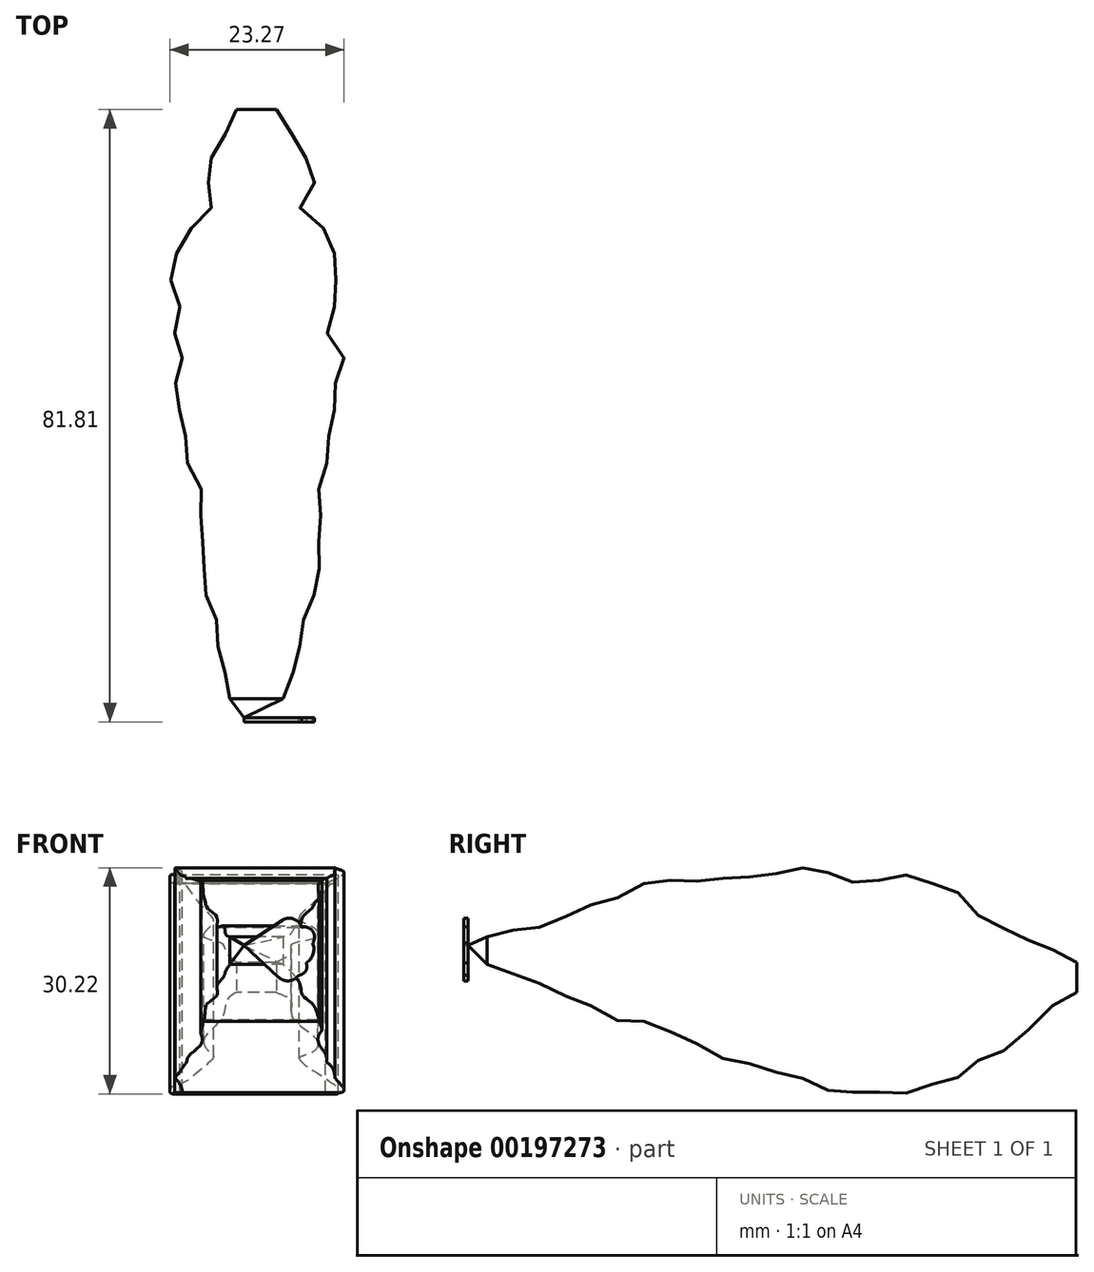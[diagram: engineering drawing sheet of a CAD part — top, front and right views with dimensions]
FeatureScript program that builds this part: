
annotation { "Feature Type Name" : "Feature", "Feature Type Description" : "" }
export const myFeature = defineFeature(function(context is Context, id is Id, definition is map)
    precondition{}
    {
        {
            var Q0;
            Q0=qCreatedBy(makeId("Front.planeOp"),FACE);
            var sketch = newSketch(context, id + "F0", { "sketchPlane" : qUnion([Q0])});
            skLineSegment(sketch, "E0.bottom", {"start": v(-55.22, 4.52) * mm, "end": v(-43.66, 4.52) * mm});
            skLineSegment(sketch, "E0.top", {"start": v(-55.22, -14.22) * mm, "end": v(-43.66, -14.22) * mm});
            skLineSegment(sketch, "E0.left", {"start": v(-55.22, 4.52) * mm, "end": v(-55.22, -14.22) * mm});
            skLineSegment(sketch, "E0.right", {"start": v(-43.66, 4.52) * mm, "end": v(-43.66, -14.22) * mm});
            skSolve(sketch);
        }
        {
            var Q0;
            Q0=qCreatedBy(makeId("Front.planeOp"),FACE);
            cPlane(context, id + "F1", {"entities" : qUnion([Q0]), "cplaneType" : CPlaneType.OFFSET, "offset" : 2.54 * mm, "width" : 152.4 * mm, "height" : 152.4 * mm});
        }
        {
            var Q0;
            Q0=qCreatedBy(id+"F1.planeOp",FACE);
            var sketch = newSketch(context, id + "F2", { "sketchPlane" : qUnion([Q0])});
            skLineSegment(sketch, "E1.bottom", {"start": v(-57.62, 7.3) * mm, "end": v(-41, 7.3) * mm});
            skLineSegment(sketch, "E1.top", {"start": v(-57.62, -16.35) * mm, "end": v(-41, -16.35) * mm});
            skLineSegment(sketch, "E1.left", {"start": v(-57.62, 7.3) * mm, "end": v(-57.62, -16.35) * mm});
            skLineSegment(sketch, "E1.right", {"start": v(-41, 7.3) * mm, "end": v(-41, -16.35) * mm});
            skSolve(sketch);
        }
        {
            var Q0;
            Q0=qCreatedBy(id+"F1.planeOp",FACE);
            cPlane(context, id + "F3", {"entities" : qUnion([Q0]), "cplaneType" : CPlaneType.OFFSET, "offset" : 2.54 * mm, "width" : 152.4 * mm, "height" : 152.4 * mm});
        }
        {
            var Q0;
            Q0=qCreatedBy(id+"F3.planeOp",FACE);
            var sketch = newSketch(context, id + "F4", { "sketchPlane" : qUnion([Q0])});
            skLineSegment(sketch, "E2.bottom", {"start": v(-39.37, 9.18) * mm, "end": v(-59.18, 9.18) * mm});
            skLineSegment(sketch, "E2.top", {"start": v(-39.37, -17.46) * mm, "end": v(-59.18, -17.46) * mm});
            skLineSegment(sketch, "E2.left", {"start": v(-39.37, 9.18) * mm, "end": v(-39.37, -17.46) * mm});
            skLineSegment(sketch, "E2.right", {"start": v(-59.18, 9.18) * mm, "end": v(-59.18, -17.46) * mm});
            skSolve(sketch);
        }
        {
            var Q0;
            Q0=qCreatedBy(id+"F3.planeOp",FACE);
            cPlane(context, id + "F5", {"entities" : qUnion([Q0]), "cplaneType" : CPlaneType.OFFSET, "offset" : 2.54 * mm, "width" : 152.4 * mm, "height" : 152.4 * mm});
        }
        {
            var Q0;
            Q0=qCreatedBy(id+"F5.planeOp",FACE);
            var sketch = newSketch(context, id + "F6", { "sketchPlane" : qUnion([Q0])});
            skLineSegment(sketch, "E3.bottom", {"start": v(-38.88, -17.91) * mm, "end": v(-60.62, -17.91) * mm});
            skLineSegment(sketch, "E3.top", {"start": v(-38.88, 9.23) * mm, "end": v(-60.62, 9.23) * mm});
            skLineSegment(sketch, "E3.left", {"start": v(-38.88, -17.91) * mm, "end": v(-38.88, 9.23) * mm});
            skLineSegment(sketch, "E3.right", {"start": v(-60.62, -17.91) * mm, "end": v(-60.62, 9.23) * mm});
            skSolve(sketch);
        }
        {
            var Q0;
            Q0=qCreatedBy(id+"F5.planeOp",FACE);
            cPlane(context, id + "F7", {"entities" : qUnion([Q0]), "cplaneType" : CPlaneType.OFFSET, "offset" : 2.54 * mm, "width" : 152.4 * mm, "height" : 152.4 * mm});
        }
        {
            var Q0;
            Q0=qCreatedBy(id+"F7.planeOp",FACE);
            var sketch = newSketch(context, id + "F8", { "sketchPlane" : qUnion([Q0])});
            skLineSegment(sketch, "E4.bottom", {"start": v(-60.8, 10.33) * mm, "end": v(-38.76, 10.33) * mm});
            skLineSegment(sketch, "E4.top", {"start": v(-60.8, -18.88) * mm, "end": v(-38.76, -18.88) * mm});
            skLineSegment(sketch, "E4.left", {"start": v(-60.8, 10.33) * mm, "end": v(-60.8, -18.88) * mm});
            skLineSegment(sketch, "E4.right", {"start": v(-38.76, 10.33) * mm, "end": v(-38.76, -18.88) * mm});
            skSolve(sketch);
        }
        {
            var Q0;
            Q0=qCreatedBy(id+"F7.planeOp",FACE);
            cPlane(context, id + "F9", {"entities" : qUnion([Q0]), "cplaneType" : CPlaneType.OFFSET, "offset" : 2.54 * mm, "width" : 152.4 * mm, "height" : 152.4 * mm});
        }
        {
            var Q0;
            Q0=qCreatedBy(id+"F9.planeOp",FACE);
            var sketch = newSketch(context, id + "F10", { "sketchPlane" : qUnion([Q0])});
            skLineSegment(sketch, "E5.bottom", {"start": v(-38.55, 9.84) * mm, "end": v(-59.66, 9.84) * mm});
            skLineSegment(sketch, "E5.top", {"start": v(-38.55, -18.76) * mm, "end": v(-59.66, -18.76) * mm});
            skLineSegment(sketch, "E5.left", {"start": v(-38.55, 9.84) * mm, "end": v(-38.55, -18.76) * mm});
            skLineSegment(sketch, "E5.right", {"start": v(-59.66, 9.84) * mm, "end": v(-59.66, -18.76) * mm});
            skSolve(sketch);
        }
        {
            var Q0;
            Q0=qCreatedBy(id+"F9.planeOp",FACE);
            cPlane(context, id + "F11", {"entities" : qUnion([Q0]), "cplaneType" : CPlaneType.OFFSET, "offset" : 2.54 * mm, "width" : 152.4 * mm, "height" : 152.4 * mm});
        }
        {
            var Q0;
            Q0=qCreatedBy(id+"F11.planeOp",FACE);
            var sketch = newSketch(context, id + "F12", { "sketchPlane" : qUnion([Q0])});
            skLineSegment(sketch, "E6.bottom", {"start": v(-39.98, 9.35) * mm, "end": v(-60.01, 9.35) * mm});
            skLineSegment(sketch, "E6.top", {"start": v(-39.98, -18.7) * mm, "end": v(-60.01, -18.7) * mm});
            skLineSegment(sketch, "E6.left", {"start": v(-39.98, 9.35) * mm, "end": v(-39.98, -18.7) * mm});
            skLineSegment(sketch, "E6.right", {"start": v(-60.01, 9.35) * mm, "end": v(-60.01, -18.7) * mm});
            skSolve(sketch);
        }
        {
            var Q0;
            Q0=qCreatedBy(id+"F11.planeOp",FACE);
            cPlane(context, id + "F13", {"entities" : qUnion([Q0]), "cplaneType" : CPlaneType.OFFSET, "offset" : 2.54 * mm, "width" : 152.4 * mm, "height" : 152.4 * mm});
        }
        {
            var Q0;
            Q0=qCreatedBy(id+"F13.planeOp",FACE);
            var sketch = newSketch(context, id + "F14", { "sketchPlane" : qUnion([Q0])});
            skLineSegment(sketch, "E7.bottom", {"start": v(-39.61, 9.47) * mm, "end": v(-60.23, 9.47) * mm});
            skLineSegment(sketch, "E7.top", {"start": v(-39.61, -18.76) * mm, "end": v(-60.23, -18.76) * mm});
            skLineSegment(sketch, "E7.left", {"start": v(-39.61, 9.47) * mm, "end": v(-39.61, -18.76) * mm});
            skLineSegment(sketch, "E7.right", {"start": v(-60.23, 9.47) * mm, "end": v(-60.23, -18.76) * mm});
            skSolve(sketch);
        }
        {
            var Q0;
            Q0=qCreatedBy(id+"F13.planeOp",FACE);
            cPlane(context, id + "F15", {"entities" : qUnion([Q0]), "cplaneType" : CPlaneType.OFFSET, "offset" : 2.54 * mm, "width" : 152.4 * mm, "height" : 152.4 * mm});
        }
        {
            var Q0;
            Q0=qCreatedBy(id+"F15.planeOp",FACE);
            var sketch = newSketch(context, id + "F16", { "sketchPlane" : qUnion([Q0])});
            skLineSegment(sketch, "E8.bottom", {"start": v(-37.71, 10.54) * mm, "end": v(-59.31, 10.54) * mm});
            skLineSegment(sketch, "E8.top", {"start": v(-37.71, -18.56) * mm, "end": v(-59.31, -18.56) * mm});
            skLineSegment(sketch, "E8.left", {"start": v(-37.71, 10.54) * mm, "end": v(-37.71, -18.56) * mm});
            skLineSegment(sketch, "E8.right", {"start": v(-59.31, 10.54) * mm, "end": v(-59.31, -18.56) * mm});
            skSolve(sketch);
        }
        {
            var Q0;
            Q0=qCreatedBy(id+"F15.planeOp",FACE);
            cPlane(context, id + "F17", {"entities" : qUnion([Q0]), "cplaneType" : CPlaneType.OFFSET, "offset" : 2.54 * mm, "width" : 152.4 * mm, "height" : 152.4 * mm});
        }
        {
            var Q0;
            Q0=qCreatedBy(id+"F17.planeOp",FACE);
            var sketch = newSketch(context, id + "F18", { "sketchPlane" : qUnion([Q0])});
            skLineSegment(sketch, "E9.bottom", {"start": v(-59.97, -17.16) * mm, "end": v(-38.63, -17.16) * mm});
            skLineSegment(sketch, "E9.top", {"start": v(-59.97, 11.13) * mm, "end": v(-38.63, 11.13) * mm});
            skLineSegment(sketch, "E9.left", {"start": v(-59.97, -17.16) * mm, "end": v(-59.97, 11.13) * mm});
            skLineSegment(sketch, "E9.right", {"start": v(-38.63, -17.16) * mm, "end": v(-38.63, 11.13) * mm});
            skSolve(sketch);
        }
        {
            var Q0;
            Q0=qCreatedBy(id+"F17.planeOp",FACE);
            cPlane(context, id + "F19", {"entities" : qUnion([Q0]), "cplaneType" : CPlaneType.OFFSET, "offset" : 2.54 * mm, "width" : 152.4 * mm, "height" : 152.4 * mm});
        }
        {
            var Q0;
            Q0=qCreatedBy(id+"F19.planeOp",FACE);
            cPlane(context, id + "F20", {"entities" : qUnion([Q0]), "cplaneType" : CPlaneType.OFFSET, "offset" : 2.54 * mm, "width" : 152.4 * mm, "height" : 152.4 * mm});
        }
        {
            var Q0;
            Q0=qCreatedBy(id+"F19.planeOp",FACE);
            var sketch = newSketch(context, id + "F21", { "sketchPlane" : qUnion([Q0])});
            skLineSegment(sketch, "E10.bottom", {"start": v(-60.2, -16.65) * mm, "end": v(-38.94, -16.65) * mm});
            skLineSegment(sketch, "E10.top", {"start": v(-60.2, 11.18) * mm, "end": v(-38.94, 11.18) * mm});
            skLineSegment(sketch, "E10.left", {"start": v(-60.2, -16.65) * mm, "end": v(-60.2, 11.18) * mm});
            skLineSegment(sketch, "E10.right", {"start": v(-38.94, -16.65) * mm, "end": v(-38.94, 11.18) * mm});
            skSolve(sketch);
        }
        {
            var Q0;
            Q0=qCreatedBy(id+"F20.planeOp",FACE);
            var sketch = newSketch(context, id + "F22", { "sketchPlane" : qUnion([Q0])});
            skLineSegment(sketch, "E11.bottom", {"start": v(-59.53, -15.85) * mm, "end": v(-39.07, -15.85) * mm});
            skLineSegment(sketch, "E11.top", {"start": v(-59.53, 10.35) * mm, "end": v(-39.07, 10.35) * mm});
            skLineSegment(sketch, "E11.left", {"start": v(-59.53, -15.85) * mm, "end": v(-59.53, 10.35) * mm});
            skLineSegment(sketch, "E11.right", {"start": v(-39.07, -15.85) * mm, "end": v(-39.07, 10.35) * mm});
            skSolve(sketch);
        }
        {
            var Q0;
            Q0=qCreatedBy(id+"F20.planeOp",FACE);
            cPlane(context, id + "F23", {"entities" : qUnion([Q0]), "cplaneType" : CPlaneType.OFFSET, "offset" : 2.54 * mm, "width" : 152.4 * mm, "height" : 152.4 * mm});
        }
        {
            var Q0;
            Q0=qCreatedBy(id+"F23.planeOp",FACE);
            var sketch = newSketch(context, id + "F24", { "sketchPlane" : qUnion([Q0])});
            skLineSegment(sketch, "E12.bottom", {"start": v(-58.95, -14.98) * mm, "end": v(-39.63, -14.98) * mm});
            skLineSegment(sketch, "E12.top", {"start": v(-58.95, 10.1) * mm, "end": v(-39.63, 10.1) * mm});
            skLineSegment(sketch, "E12.left", {"start": v(-58.95, -14.98) * mm, "end": v(-58.95, 10.1) * mm});
            skLineSegment(sketch, "E12.right", {"start": v(-39.63, -14.98) * mm, "end": v(-39.63, 10.1) * mm});
            skSolve(sketch);
        }
        {
            var Q0;
            Q0=qCreatedBy(id+"F23.planeOp",FACE);
            cPlane(context, id + "F25", {"entities" : qUnion([Q0]), "cplaneType" : CPlaneType.OFFSET, "offset" : 2.54 * mm, "width" : 152.4 * mm, "height" : 152.4 * mm});
        }
        {
            var Q0;
            Q0=qCreatedBy(id+"F25.planeOp",FACE);
            var sketch = newSketch(context, id + "F26", { "sketchPlane" : qUnion([Q0])});
            skLineSegment(sketch, "E13.bottom", {"start": v(-58.7, -14.62) * mm, "end": v(-40.03, -14.62) * mm});
            skLineSegment(sketch, "E13.top", {"start": v(-58.7, 9.76) * mm, "end": v(-40.03, 9.76) * mm});
            skLineSegment(sketch, "E13.left", {"start": v(-58.7, -14.62) * mm, "end": v(-58.7, 9.76) * mm});
            skLineSegment(sketch, "E13.right", {"start": v(-40.03, -14.62) * mm, "end": v(-40.03, 9.76) * mm});
            skSolve(sketch);
        }
        {
            var Q0;
            Q0=qCreatedBy(id+"F25.planeOp",FACE);
            cPlane(context, id + "F27", {"entities" : qUnion([Q0]), "cplaneType" : CPlaneType.OFFSET, "offset" : 2.54 * mm, "width" : 152.4 * mm, "height" : 152.4 * mm});
        }
        {
            var Q0;
            Q0=qCreatedBy(id+"F27.planeOp",FACE);
            var sketch = newSketch(context, id + "F28", { "sketchPlane" : qUnion([Q0])});
            skLineSegment(sketch, "E14.bottom", {"start": v(-58.28, -13.75) * mm, "end": v(-40.1, -13.75) * mm});
            skLineSegment(sketch, "E14.top", {"start": v(-58.28, 9.86) * mm, "end": v(-40.1, 9.86) * mm});
            skLineSegment(sketch, "E14.left", {"start": v(-58.28, -13.75) * mm, "end": v(-58.28, 9.86) * mm});
            skLineSegment(sketch, "E14.right", {"start": v(-40.1, -13.75) * mm, "end": v(-40.1, 9.86) * mm});
            skSolve(sketch);
        }
        {
            var Q0;
            Q0=qCreatedBy(id+"F27.planeOp",FACE);
            cPlane(context, id + "F29", {"entities" : qUnion([Q0]), "cplaneType" : CPlaneType.OFFSET, "offset" : 2.54 * mm, "width" : 152.4 * mm, "height" : 152.4 * mm});
        }
        {
            var Q0;
            Q0=qCreatedBy(id+"F29.planeOp",FACE);
            var sketch = newSketch(context, id + "F30", { "sketchPlane" : qUnion([Q0])});
            skLineSegment(sketch, "E15.bottom", {"start": v(-56.71, -12.18) * mm, "end": v(-41.08, -12.18) * mm});
            skLineSegment(sketch, "E15.top", {"start": v(-56.71, 9.43) * mm, "end": v(-41.08, 9.43) * mm});
            skLineSegment(sketch, "E15.left", {"start": v(-56.71, -12.18) * mm, "end": v(-56.71, 9.43) * mm});
            skLineSegment(sketch, "E15.right", {"start": v(-41.08, -12.18) * mm, "end": v(-41.08, 9.43) * mm});
            skSolve(sketch);
        }
        {
            var Q0;
            Q0=qCreatedBy(id+"F29.planeOp",FACE);
            var Q1;
            Q1 = qBodyType(qCreatedBy(id + "F32" ,EDGE), BodyType.WIRE);
            cPlane(context, id + "F31", {"entities" : qUnion([Q0, Q1]), "cplaneType" : CPlaneType.OFFSET, "offset" : 2.54 * mm, "width" : 152.4 * mm, "height" : 152.4 * mm});
        }
        {
            var Q0;
            Q0=qCreatedBy(id+"F31.planeOp",FACE);
            var sketch = newSketch(context, id + "F32", { "sketchPlane" : qUnion([Q0])});
            skLineSegment(sketch, "E16.bottom", {"start": v(-56.81, -10.9) * mm, "end": v(-40.98, -10.9) * mm});
            skLineSegment(sketch, "E16.top", {"start": v(-56.81, 9.56) * mm, "end": v(-40.98, 9.56) * mm});
            skLineSegment(sketch, "E16.left", {"start": v(-56.81, -10.9) * mm, "end": v(-56.81, 9.56) * mm});
            skLineSegment(sketch, "E16.right", {"start": v(-40.98, -10.9) * mm, "end": v(-40.98, 9.56) * mm});
            skSolve(sketch);
        }
        {
            var Q0;
            Q0=qCreatedBy(id+"F31.planeOp",FACE);
            cPlane(context, id + "F33", {"entities" : qUnion([Q0]), "cplaneType" : CPlaneType.OFFSET, "offset" : 2.54 * mm, "width" : 152.4 * mm, "height" : 152.4 * mm});
        }
        {
            var Q0;
            Q0=qCreatedBy(id+"F33.planeOp",FACE);
            var sketch = newSketch(context, id + "F34", { "sketchPlane" : qUnion([Q0])});
            skLineSegment(sketch, "E17.bottom", {"start": v(-40.67, 9.48) * mm, "end": v(-56.64, 9.48) * mm});
            skLineSegment(sketch, "E17.top", {"start": v(-40.67, -10.2) * mm, "end": v(-56.64, -10.2) * mm});
            skLineSegment(sketch, "E17.left", {"start": v(-40.67, 9.48) * mm, "end": v(-40.67, -10.2) * mm});
            skLineSegment(sketch, "E17.right", {"start": v(-56.64, 9.48) * mm, "end": v(-56.64, -10.2) * mm});
            skSolve(sketch);
        }
        {
            var Q0;
            Q0=qCreatedBy(id+"F33.planeOp",FACE);
            cPlane(context, id + "F35", {"entities" : qUnion([Q0]), "cplaneType" : CPlaneType.OFFSET, "offset" : 2.54 * mm, "width" : 152.4 * mm, "height" : 152.4 * mm});
        }
        {
            var Q0;
            Q0=qCreatedBy(id+"F35.planeOp",FACE);
            var sketch = newSketch(context, id + "F36", { "sketchPlane" : qUnion([Q0])});
            skLineSegment(sketch, "E18.bottom", {"start": v(-41.15, 8.93) * mm, "end": v(-56.56, 8.93) * mm});
            skLineSegment(sketch, "E18.top", {"start": v(-41.15, -9.09) * mm, "end": v(-56.56, -9.09) * mm});
            skLineSegment(sketch, "E18.left", {"start": v(-41.15, 8.93) * mm, "end": v(-41.15, -9.09) * mm});
            skLineSegment(sketch, "E18.right", {"start": v(-56.56, 8.93) * mm, "end": v(-56.56, -9.09) * mm});
            skSolve(sketch);
        }
        {
            var Q0;
            Q0=qCreatedBy(id+"F35.planeOp",FACE);
            cPlane(context, id + "F37", {"entities" : qUnion([Q0]), "cplaneType" : CPlaneType.OFFSET, "offset" : 2.54 * mm, "width" : 152.4 * mm, "height" : 152.4 * mm});
        }
        {
            var Q0;
            Q0=qCreatedBy(id+"F37.planeOp",FACE);
            var sketch = newSketch(context, id + "F38", { "sketchPlane" : qUnion([Q0])});
            skLineSegment(sketch, "E19.bottom", {"start": v(-40.99, 7.37) * mm, "end": v(-56.4, 7.37) * mm});
            skLineSegment(sketch, "E19.top", {"start": v(-40.99, -9.24) * mm, "end": v(-56.4, -9.24) * mm});
            skLineSegment(sketch, "E19.left", {"start": v(-40.99, 7.37) * mm, "end": v(-40.99, -9.24) * mm});
            skLineSegment(sketch, "E19.right", {"start": v(-56.4, 7.37) * mm, "end": v(-56.4, -9.24) * mm});
            skSolve(sketch);
        }
        {
            var Q0;
            Q0=qCreatedBy(id+"F37.planeOp",FACE);
            cPlane(context, id + "F39", {"entities" : qUnion([Q0]), "cplaneType" : CPlaneType.OFFSET, "offset" : 2.54 * mm, "width" : 152.4 * mm, "height" : 152.4 * mm});
        }
        {
            var Q0;
            Q0=qCreatedBy(id+"F39.planeOp",FACE);
            var sketch = newSketch(context, id + "F40", { "sketchPlane" : qUnion([Q0])});
            skLineSegment(sketch, "E20.bottom", {"start": v(-41.44, 6.78) * mm, "end": v(-56.23, 6.78) * mm});
            skLineSegment(sketch, "E20.top", {"start": v(-41.44, -7.76) * mm, "end": v(-56.23, -7.76) * mm});
            skLineSegment(sketch, "E20.left", {"start": v(-41.44, 6.78) * mm, "end": v(-41.44, -7.76) * mm});
            skLineSegment(sketch, "E20.right", {"start": v(-56.23, 6.78) * mm, "end": v(-56.23, -7.76) * mm});
            skSolve(sketch);
        }
        {
            var Q0;
            Q0=qCreatedBy(id+"F39.planeOp",FACE);
            cPlane(context, id + "F41", {"entities" : qUnion([Q0]), "cplaneType" : CPlaneType.OFFSET, "offset" : 2.54 * mm, "width" : 152.4 * mm, "height" : 152.4 * mm});
        }
        {
            var Q0;
            Q0=qCreatedBy(id+"F41.planeOp",FACE);
            var sketch = newSketch(context, id + "F42", { "sketchPlane" : qUnion([Q0])});
            skLineSegment(sketch, "E21.bottom", {"start": v(-42.05, 5.8) * mm, "end": v(-55.87, 5.8) * mm});
            skLineSegment(sketch, "E21.top", {"start": v(-42.05, -6.79) * mm, "end": v(-55.87, -6.79) * mm});
            skLineSegment(sketch, "E21.left", {"start": v(-42.05, 5.8) * mm, "end": v(-42.05, -6.79) * mm});
            skLineSegment(sketch, "E21.right", {"start": v(-55.87, 5.8) * mm, "end": v(-55.87, -6.79) * mm});
            skSolve(sketch);
        }
        {
            var Q0;
            Q0=qCreatedBy(id+"F41.planeOp",FACE);
            cPlane(context, id + "F43", {"entities" : qUnion([Q0]), "cplaneType" : CPlaneType.OFFSET, "offset" : 2.54 * mm, "width" : 152.4 * mm, "height" : 152.4 * mm});
        }
        {
            var Q0;
            Q0=qCreatedBy(id+"F43.planeOp",FACE);
            var sketch = newSketch(context, id + "F44", { "sketchPlane" : qUnion([Q0])});
            skLineSegment(sketch, "E22.bottom", {"start": v(-43.28, 4.58) * mm, "end": v(-54.64, 4.58) * mm});
            skLineSegment(sketch, "E22.top", {"start": v(-43.28, -5.69) * mm, "end": v(-54.64, -5.69) * mm});
            skLineSegment(sketch, "E22.left", {"start": v(-43.28, 4.58) * mm, "end": v(-43.28, -5.69) * mm});
            skLineSegment(sketch, "E22.right", {"start": v(-54.64, 4.58) * mm, "end": v(-54.64, -5.69) * mm});
            skSolve(sketch);
        }
        {
            var Q0;
            Q0=qCreatedBy(id+"F43.planeOp",FACE);
            cPlane(context, id + "F45", {"entities" : qUnion([Q0]), "cplaneType" : CPlaneType.OFFSET, "offset" : 2.54 * mm, "width" : 152.4 * mm, "height" : 152.4 * mm});
        }
        {
            var Q0;
            Q0=qCreatedBy(id+"F45.planeOp",FACE);
            var sketch = newSketch(context, id + "F46", { "sketchPlane" : qUnion([Q0])});
            skLineSegment(sketch, "E23.bottom", {"start": v(-43.52, 3.36) * mm, "end": v(-54.64, 3.36) * mm});
            skLineSegment(sketch, "E23.top", {"start": v(-43.52, -4.46) * mm, "end": v(-54.64, -4.46) * mm});
            skLineSegment(sketch, "E23.left", {"start": v(-43.52, 3.36) * mm, "end": v(-43.52, -4.46) * mm});
            skLineSegment(sketch, "E23.right", {"start": v(-54.64, 3.36) * mm, "end": v(-54.64, -4.46) * mm});
            skSolve(sketch);
        }
        {
            var Q0;
            Q0=qCreatedBy(id+"F45.planeOp",FACE);
            cPlane(context, id + "F47", {"entities" : qUnion([Q0]), "cplaneType" : CPlaneType.OFFSET, "offset" : 2.54 * mm, "width" : 152.4 * mm, "height" : 152.4 * mm});
        }
        {
            var Q0;
            Q0=qCreatedBy(id+"F47.planeOp",FACE);
            var sketch = newSketch(context, id + "F48", { "sketchPlane" : qUnion([Q0])});
            skLineSegment(sketch, "E24.bottom", {"start": v(-44.13, 3.48) * mm, "end": v(-53.79, 3.48) * mm});
            skLineSegment(sketch, "E24.top", {"start": v(-44.13, -3.36) * mm, "end": v(-53.79, -3.36) * mm});
            skLineSegment(sketch, "E24.left", {"start": v(-44.13, 3.48) * mm, "end": v(-44.13, -3.36) * mm});
            skLineSegment(sketch, "E24.right", {"start": v(-53.79, 3.48) * mm, "end": v(-53.79, -3.36) * mm});
            skSolve(sketch);
        }
        {
            var Q0;
            Q0=qCreatedBy(id+"F47.planeOp",FACE);
            cPlane(context, id + "F49", {"entities" : qUnion([Q0]), "cplaneType" : CPlaneType.OFFSET, "offset" : 2.54 * mm, "width" : 152.4 * mm, "height" : 152.4 * mm});
        }
        {
            var Q0;
            Q0=qCreatedBy(id+"F49.planeOp",FACE);
            var sketch = newSketch(context, id + "F50", { "sketchPlane" : qUnion([Q0])});
            skLineSegment(sketch, "E25.bottom", {"start": v(-44.74, 2.5) * mm, "end": v(-53.54, 2.5) * mm});
            skLineSegment(sketch, "E25.top", {"start": v(-44.74, -2.63) * mm, "end": v(-53.54, -2.63) * mm});
            skLineSegment(sketch, "E25.left", {"start": v(-44.74, 2.5) * mm, "end": v(-44.74, -2.63) * mm});
            skLineSegment(sketch, "E25.right", {"start": v(-53.54, 2.5) * mm, "end": v(-53.54, -2.63) * mm});
            skSolve(sketch);
        }
        {
            var Q0;
            Q0=qCreatedBy(id+"F49.planeOp",FACE);
            cPlane(context, id + "F51", {"entities" : qUnion([Q0]), "cplaneType" : CPlaneType.OFFSET, "offset" : 2.54 * mm, "width" : 152.4 * mm, "height" : 152.4 * mm});
        }
        {
            var Q0;
            Q0=qCreatedBy(id+"F51.planeOp",FACE);
            var sketch = newSketch(context, id + "F52", { "sketchPlane" : qUnion([Q0])});
            skLineSegment(sketch, "E26.bottom", {"start": v(-45.84, 2.02) * mm, "end": v(-52.93, 2.02) * mm});
            skLineSegment(sketch, "E26.top", {"start": v(-45.84, -1.65) * mm, "end": v(-52.93, -1.65) * mm});
            skLineSegment(sketch, "E26.left", {"start": v(-45.84, 2.02) * mm, "end": v(-45.84, -1.65) * mm});
            skLineSegment(sketch, "E26.right", {"start": v(-52.93, 2.02) * mm, "end": v(-52.93, -1.65) * mm});
            skSolve(sketch);
        }
        {
            var Q0;
            Q0=qCreatedBy(makeId("Front.planeOp"),FACE);
            cPlane(context, id + "F53", {"entities" : qUnion([Q0]), "cplaneType" : CPlaneType.OFFSET, "offset" : 2.54 * mm, "oppositeDirection" : true, "width" : 152.4 * mm, "height" : 152.4 * mm});
        }
        {
            var Q0;
            Q0=qCreatedBy(id+"F53.planeOp",FACE);
            var sketch = newSketch(context, id + "F54", { "sketchPlane" : qUnion([Q0])});
            skLineSegment(sketch, "E27.bottom", {"start": v(-55.62, 3.36) * mm, "end": v(-41.93, 3.36) * mm});
            skLineSegment(sketch, "E27.top", {"start": v(-55.62, -13.39) * mm, "end": v(-41.93, -13.39) * mm});
            skLineSegment(sketch, "E27.left", {"start": v(-55.62, 3.36) * mm, "end": v(-55.62, -13.39) * mm});
            skLineSegment(sketch, "E27.right", {"start": v(-41.93, 3.36) * mm, "end": v(-41.93, -13.39) * mm});
            skSolve(sketch);
        }
        {
            var Q0;
            Q0=qCreatedBy(id+"F53.planeOp",FACE);
            cPlane(context, id + "F55", {"entities" : qUnion([Q0]), "cplaneType" : CPlaneType.OFFSET, "offset" : 2.54 * mm, "oppositeDirection" : true, "width" : 152.4 * mm, "height" : 152.4 * mm});
        }
        {
            var Q0;
            Q0=qCreatedBy(id+"F55.planeOp",FACE);
            var sketch = newSketch(context, id + "F56", { "sketchPlane" : qUnion([Q0])});
            skLineSegment(sketch, "E28.bottom", {"start": v(-56.36, 2.02) * mm, "end": v(-41.44, 2.02) * mm});
            skLineSegment(sketch, "E28.top", {"start": v(-56.36, -11.55) * mm, "end": v(-41.44, -11.55) * mm});
            skLineSegment(sketch, "E28.left", {"start": v(-56.36, 2.02) * mm, "end": v(-56.36, -11.55) * mm});
            skLineSegment(sketch, "E28.right", {"start": v(-41.44, 2.02) * mm, "end": v(-41.44, -11.55) * mm});
            skSolve(sketch);
        }
        {
            var Q0;
            Q0=qCreatedBy(id+"F55.planeOp",FACE);
            cPlane(context, id + "F57", {"entities" : qUnion([Q0]), "cplaneType" : CPlaneType.OFFSET, "offset" : 2.54 * mm, "oppositeDirection" : true, "width" : 152.4 * mm, "height" : 152.4 * mm});
        }
        {
            var Q0;
            Q0=qCreatedBy(id+"F57.planeOp",FACE);
            var sketch = newSketch(context, id + "F58", { "sketchPlane" : qUnion([Q0])});
            skLineSegment(sketch, "E29.bottom", {"start": v(-54.03, 1.16) * mm, "end": v(-44.5, 1.16) * mm});
            skLineSegment(sketch, "E29.top", {"start": v(-54.03, -8.86) * mm, "end": v(-44.5, -8.86) * mm});
            skLineSegment(sketch, "E29.left", {"start": v(-54.03, 1.16) * mm, "end": v(-54.03, -8.86) * mm});
            skLineSegment(sketch, "E29.right", {"start": v(-44.5, 1.16) * mm, "end": v(-44.5, -8.86) * mm});
            skSolve(sketch);
        }
        {
            var Q0;
            Q0=qCreatedBy(id+"F57.planeOp",FACE);
            cPlane(context, id + "F59", {"entities" : qUnion([Q0]), "cplaneType" : CPlaneType.OFFSET, "offset" : 2.54 * mm, "oppositeDirection" : true, "width" : 152.4 * mm, "height" : 152.4 * mm});
        }
        {
            var Q0;
            Q0=qCreatedBy(id+"F59.planeOp",FACE);
            var sketch = newSketch(context, id + "F60", { "sketchPlane" : qUnion([Q0])});
            skLineSegment(sketch, "E30.bottom", {"start": v(-53.42, 0) * mm, "end": v(-44.74, 0) * mm});
            skLineSegment(sketch, "E30.top", {"start": v(-53.42, -6.66) * mm, "end": v(-44.74, -6.66) * mm});
            skLineSegment(sketch, "E30.left", {"start": v(-53.42, 0) * mm, "end": v(-53.42, -6.66) * mm});
            skLineSegment(sketch, "E30.right", {"start": v(-44.74, 0) * mm, "end": v(-44.74, -6.66) * mm});
            skSolve(sketch);
        }
        {
            var Q0;
            Q0=qCreatedBy(id+"F59.planeOp",FACE);
            cPlane(context, id + "F61", {"entities" : qUnion([Q0]), "cplaneType" : CPlaneType.OFFSET, "offset" : 2.54 * mm, "oppositeDirection" : true, "width" : 152.4 * mm, "height" : 152.4 * mm});
        }
        {
            var Q0;
            Q0=qCreatedBy(id+"F61.planeOp",FACE);
            var sketch = newSketch(context, id + "F62", { "sketchPlane" : qUnion([Q0])});
            skLineSegment(sketch, "E31.bottom", {"start": v(-46.74, -1.36) * mm, "end": v(-52.08, -1.36) * mm});
            skLineSegment(sketch, "E31.top", {"start": v(-46.74, -5.4) * mm, "end": v(-52.08, -5.4) * mm});
            skLineSegment(sketch, "E31.left", {"start": v(-46.74, -1.36) * mm, "end": v(-46.74, -5.4) * mm});
            skLineSegment(sketch, "E31.right", {"start": v(-52.08, -1.36) * mm, "end": v(-52.08, -5.4) * mm});
            skSolve(sketch);
        }
        {
            var Q0;
            Q0=qCreatedBy(id+"F51.planeOp",FACE);
            cPlane(context, id + "F63", {"entities" : qUnion([Q0]), "cplaneType" : CPlaneType.OFFSET, "offset" : 2.54 * mm, "width" : 152.4 * mm, "height" : 152.4 * mm});
        }
        {
            var Q0;
            Q0=qCreatedBy(id+"F63.planeOp",FACE);
            var sketch = newSketch(context, id + "F64", { "sketchPlane" : qUnion([Q0])});
            skLineSegment(sketch, "E32", {"start": v(-51.07, 0.87) * mm, "end": v(-43.4, 3.3) * mm});
            skLineSegment(sketch, "E33", {"start": v(-51.07, 0.87) * mm, "end": v(-41.87, 1.22) * mm});
            skLineSegment(sketch, "E34", {"start": v(-51.07, 0.87) * mm, "end": v(-42.74, -1.44) * mm});
            skLineSegment(sketch, "E35", {"start": v(-51.07, 0.87) * mm, "end": v(-46.44, -3.36) * mm});
            skLineSegment(sketch, "E36", {"start": v(-51.07, 0.87) * mm, "end": v(-43.72, -3.1) * mm});
            skArc(sketch, "E37", {"start": v(-41.87, 1.22) * mm, "mid": v(-41.89, 2.8) * mm, "end": v(-43.4, 3.3) * mm});
            skArc(sketch, "E38", {"start": v(-42.74, -1.44) * mm, "mid": v(-41.84, -0.26) * mm, "end": v(-41.87, 1.22) * mm});
            skArc(sketch, "E39", {"start": v(-43.72, -3.1) * mm, "mid": v(-42.82, -2.5) * mm, "end": v(-42.74, -1.44) * mm});
            skArc(sketch, "E40", {"start": v(-46.44, -3.36) * mm, "mid": v(-45.02, -3.84) * mm, "end": v(-43.72, -3.1) * mm});
            skLineSegment(sketch, "E41", {"start": v(-51.07, 0.87) * mm, "end": v(-45.9, 4.26) * mm});
            skArc(sketch, "E42", {"start": v(-43.4, 3.3) * mm, "mid": v(-44.4, 4.42) * mm, "end": v(-45.9, 4.26) * mm});
            skSolve(sketch);
        }
        {
            var Q0;
            Q0=makeQuery(id+"F62.imprint","IMPRINT",FACE,{"disambiguationData":[TD([[makeQuery(id+"F62.imprint","IMPRINT",EDGE,{"derivedFrom":sQuery(id+"F62.wireOp",EDGE,"E31.bottom")}),1.0]])]});
            var Q1;
            Q1=makeQuery(id+"F60.imprint","IMPRINT",FACE,{"disambiguationData":[TD([[makeQuery(id+"F60.imprint","IMPRINT",EDGE,{"derivedFrom":sQuery(id+"F60.wireOp",EDGE,"E30.bottom")}),-1.0]])]});
            var Q2;
            Q2=makeQuery(id+"F58.imprint","IMPRINT",FACE,{"disambiguationData":[TD([[makeQuery(id+"F58.imprint","IMPRINT",EDGE,{"derivedFrom":sQuery(id+"F58.wireOp",EDGE,"E29.bottom")}),-1.0]])]});
            var Q3;
            Q3=makeQuery(id+"F56.imprint","IMPRINT",FACE,{"disambiguationData":[TD([[makeQuery(id+"F56.imprint","IMPRINT",EDGE,{"derivedFrom":sQuery(id+"F56.wireOp",EDGE,"E28.bottom")}),-1.0]])]});
            var Q4;
            Q4=makeQuery(id+"F54.imprint","IMPRINT",FACE,{"disambiguationData":[TD([[makeQuery(id+"F54.imprint","IMPRINT",EDGE,{"derivedFrom":sQuery(id+"F54.wireOp",EDGE,"E27.bottom")}),-1.0]])]});
            var Q5;
            Q5=makeQuery(id+"F0.imprint","IMPRINT",FACE,{"disambiguationData":[TD([[makeQuery(id+"F0.imprint","IMPRINT",EDGE,{"derivedFrom":sQuery(id+"F0.wireOp",EDGE,"E0.bottom")}),-1.0]])]});
            var Q6;
            Q6=makeQuery(id+"F2.imprint","IMPRINT",FACE,{"disambiguationData":[TD([[makeQuery(id+"F2.imprint","IMPRINT",EDGE,{"derivedFrom":sQuery(id+"F2.wireOp",EDGE,"E1.bottom")}),-1.0]])]});
            var Q7;
            Q7=makeQuery(id+"F4.imprint","IMPRINT",FACE,{"disambiguationData":[TD([[makeQuery(id+"F4.imprint","IMPRINT",EDGE,{"derivedFrom":sQuery(id+"F4.wireOp",EDGE,"E2.bottom")}),1.0]])]});
            var Q8;
            Q8=makeQuery(id+"F6.imprint","IMPRINT",FACE,{"disambiguationData":[TD([[makeQuery(id+"F6.imprint","IMPRINT",EDGE,{"derivedFrom":sQuery(id+"F6.wireOp",EDGE,"E3.bottom")}),-1.0]])]});
            var Q9;
            Q9=makeQuery(id+"F8.imprint","IMPRINT",FACE,{"disambiguationData":[TD([[makeQuery(id+"F8.imprint","IMPRINT",EDGE,{"derivedFrom":sQuery(id+"F8.wireOp",EDGE,"E4.bottom")}),-1.0]])]});
            var Q10;
            Q10=makeQuery(id+"F10.imprint","IMPRINT",FACE,{"disambiguationData":[TD([[makeQuery(id+"F10.imprint","IMPRINT",EDGE,{"derivedFrom":sQuery(id+"F10.wireOp",EDGE,"E5.bottom")}),1.0]])]});
            var Q11;
            Q11=makeQuery(id+"F12.imprint","IMPRINT",FACE,{"disambiguationData":[TD([[makeQuery(id+"F12.imprint","IMPRINT",EDGE,{"derivedFrom":sQuery(id+"F12.wireOp",EDGE,"E6.bottom")}),1.0]])]});
            var Q12;
            Q12=makeQuery(id+"F14.imprint","IMPRINT",FACE,{"disambiguationData":[TD([[makeQuery(id+"F14.imprint","IMPRINT",EDGE,{"derivedFrom":sQuery(id+"F14.wireOp",EDGE,"E7.bottom")}),1.0]])]});
            var Q13;
            Q13=makeQuery(id+"F16.imprint","IMPRINT",FACE,{"disambiguationData":[TD([[makeQuery(id+"F16.imprint","IMPRINT",EDGE,{"derivedFrom":sQuery(id+"F16.wireOp",EDGE,"E8.bottom")}),1.0]])]});
            var Q14;
            Q14=makeQuery(id+"F18.imprint","IMPRINT",FACE,{"disambiguationData":[TD([[makeQuery(id+"F18.imprint","IMPRINT",EDGE,{"derivedFrom":sQuery(id+"F18.wireOp",EDGE,"E9.bottom")}),1.0]])]});
            var Q15;
            Q15=makeQuery(id+"F21.imprint","IMPRINT",FACE,{"disambiguationData":[TD([[makeQuery(id+"F21.imprint","IMPRINT",EDGE,{"derivedFrom":sQuery(id+"F21.wireOp",EDGE,"E10.bottom")}),1.0]])]});
            var Q16;
            Q16=makeQuery(id+"F22.imprint","IMPRINT",FACE,{"disambiguationData":[TD([[makeQuery(id+"F22.imprint","IMPRINT",EDGE,{"derivedFrom":sQuery(id+"F22.wireOp",EDGE,"E11.bottom")}),1.0]])]});
            var Q17;
            Q17=makeQuery(id+"F24.imprint","IMPRINT",FACE,{"disambiguationData":[TD([[makeQuery(id+"F24.imprint","IMPRINT",EDGE,{"derivedFrom":sQuery(id+"F24.wireOp",EDGE,"E12.bottom")}),1.0]])]});
            var Q18;
            Q18=makeQuery(id+"F26.imprint","IMPRINT",FACE,{"disambiguationData":[TD([[makeQuery(id+"F26.imprint","IMPRINT",EDGE,{"derivedFrom":sQuery(id+"F26.wireOp",EDGE,"E13.bottom")}),1.0]])]});
            var Q19;
            Q19=makeQuery(id+"F28.imprint","IMPRINT",FACE,{"disambiguationData":[TD([[makeQuery(id+"F28.imprint","IMPRINT",EDGE,{"derivedFrom":sQuery(id+"F28.wireOp",EDGE,"E14.bottom")}),1.0]])]});
            var Q20;
            Q20=makeQuery(id+"F30.imprint","IMPRINT",FACE,{"disambiguationData":[TD([[makeQuery(id+"F30.imprint","IMPRINT",EDGE,{"derivedFrom":sQuery(id+"F30.wireOp",EDGE,"E15.bottom")}),1.0]])]});
            var Q21;
            Q21=makeQuery(id+"F32.imprint","IMPRINT",FACE,{"disambiguationData":[TD([[makeQuery(id+"F32.imprint","IMPRINT",EDGE,{"derivedFrom":sQuery(id+"F32.wireOp",EDGE,"E16.bottom")}),1.0]])]});
            var Q22;
            Q22=makeQuery(id+"F34.imprint","IMPRINT",FACE,{"disambiguationData":[TD([[makeQuery(id+"F34.imprint","IMPRINT",EDGE,{"derivedFrom":sQuery(id+"F34.wireOp",EDGE,"E17.bottom")}),1.0]])]});
            var Q23;
            Q23=makeQuery(id+"F36.imprint","IMPRINT",FACE,{"disambiguationData":[TD([[makeQuery(id+"F36.imprint","IMPRINT",EDGE,{"derivedFrom":sQuery(id+"F36.wireOp",EDGE,"E18.bottom")}),1.0]])]});
            var Q24;
            Q24=makeQuery(id+"F38.imprint","IMPRINT",FACE,{"disambiguationData":[TD([[makeQuery(id+"F38.imprint","IMPRINT",EDGE,{"derivedFrom":sQuery(id+"F38.wireOp",EDGE,"E19.bottom")}),1.0]])]});
            var Q25;
            Q25=makeQuery(id+"F40.imprint","IMPRINT",FACE,{"disambiguationData":[TD([[makeQuery(id+"F40.imprint","IMPRINT",EDGE,{"derivedFrom":sQuery(id+"F40.wireOp",EDGE,"E20.bottom")}),1.0]])]});
            var Q26;
            Q26=makeQuery(id+"F42.imprint","IMPRINT",FACE,{"disambiguationData":[TD([[makeQuery(id+"F42.imprint","IMPRINT",EDGE,{"derivedFrom":sQuery(id+"F42.wireOp",EDGE,"E21.bottom")}),1.0]])]});
            var Q27;
            Q27=makeQuery(id+"F44.imprint","IMPRINT",FACE,{"disambiguationData":[TD([[makeQuery(id+"F44.imprint","IMPRINT",EDGE,{"derivedFrom":sQuery(id+"F44.wireOp",EDGE,"E22.bottom")}),1.0]])]});
            var Q28;
            Q28=makeQuery(id+"F46.imprint","IMPRINT",FACE,{"disambiguationData":[TD([[makeQuery(id+"F46.imprint","IMPRINT",EDGE,{"derivedFrom":sQuery(id+"F46.wireOp",EDGE,"E23.bottom")}),1.0]])]});
            var Q29;
            Q29=makeQuery(id+"F48.imprint","IMPRINT",FACE,{"disambiguationData":[TD([[makeQuery(id+"F48.imprint","IMPRINT",EDGE,{"derivedFrom":sQuery(id+"F48.wireOp",EDGE,"E24.bottom")}),1.0]])]});
            var Q30;
            Q30=makeQuery(id+"F50.imprint","IMPRINT",FACE,{"disambiguationData":[TD([[makeQuery(id+"F50.imprint","IMPRINT",EDGE,{"derivedFrom":sQuery(id+"F50.wireOp",EDGE,"E25.bottom")}),1.0]])]});
            var Q31;
            Q31=makeQuery(id+"F52.imprint","IMPRINT",FACE,{"disambiguationData":[TD([[makeQuery(id+"F52.imprint","IMPRINT",EDGE,{"derivedFrom":sQuery(id+"F52.wireOp",EDGE,"E26.bottom")}),1.0]])]});
            loft(context, id + "F65", {"sheetProfilesArray" : [{ "sheetProfileEntities" : qUnion([Q0]) }, { "sheetProfileEntities" : qUnion([Q1]) }, { "sheetProfileEntities" : qUnion([Q2]) }, { "sheetProfileEntities" : qUnion([Q3]) }, { "sheetProfileEntities" : qUnion([Q4]) }, { "sheetProfileEntities" : qUnion([Q5]) }, { "sheetProfileEntities" : qUnion([Q6]) }, { "sheetProfileEntities" : qUnion([Q7]) }, { "sheetProfileEntities" : qUnion([Q8]) }, { "sheetProfileEntities" : qUnion([Q9]) }, { "sheetProfileEntities" : qUnion([Q10]) }, { "sheetProfileEntities" : qUnion([Q11]) }, { "sheetProfileEntities" : qUnion([Q12]) }, { "sheetProfileEntities" : qUnion([Q13]) }, { "sheetProfileEntities" : qUnion([Q14]) }, { "sheetProfileEntities" : qUnion([Q15]) }, { "sheetProfileEntities" : qUnion([Q16]) }, { "sheetProfileEntities" : qUnion([Q17]) }, { "sheetProfileEntities" : qUnion([Q18]) }, { "sheetProfileEntities" : qUnion([Q19]) }, { "sheetProfileEntities" : qUnion([Q20]) }, { "sheetProfileEntities" : qUnion([Q21]) }, { "sheetProfileEntities" : qUnion([Q22]) }, { "sheetProfileEntities" : qUnion([Q23]) }, { "sheetProfileEntities" : qUnion([Q24]) }, { "sheetProfileEntities" : qUnion([Q25]) }, { "sheetProfileEntities" : qUnion([Q26]) }, { "sheetProfileEntities" : qUnion([Q27]) }, { "sheetProfileEntities" : qUnion([Q28]) }, { "sheetProfileEntities" : qUnion([Q29]) }, { "sheetProfileEntities" : qUnion([Q30]) }, { "sheetProfileEntities" : qUnion([Q31]) }]});
        }
        {
            var Q1;
            Q1=sQuery(id+"F64.wireOp",VERTEX,"E32.start");
            var Q2;
            Q2=makeQuery(id+"F65.opLoft","CAP_FACE",FACE,{"disambiguationData":[OSD([makeQuery(id+"F52.imprint","IMPRINT",FACE,{"disambiguationData":[TD([[makeQuery(id+"F52.imprint","IMPRINT",EDGE,{"derivedFrom":sQuery(id+"F52.wireOp",EDGE,"E26.bottom")}),1.0]])]})])],"isStart":true});
            loft(context, id + "F66", {"operationType" : NewBodyOperationType.ADD, "sheetProfilesArray" : [{ "sheetProfileEntities" : qUnion([Q1]) }, { "sheetProfileEntities" : qUnion([Q2]) }]});
        }
        {
            var Q0;
            Q0=makeQuery(id+"F64.imprint","IMPRINT",FACE,{"disambiguationData":[TD([[makeQuery(id+"F64.imprint","IMPRINT",EDGE,{"derivedFrom":sQuery(id+"F64.wireOp",EDGE,"E33")}),-1.0]])]});
            var Q1;
            Q1=makeQuery(id+"F64.imprint","IMPRINT",FACE,{"disambiguationData":[TD([[makeQuery(id+"F64.imprint","IMPRINT",EDGE,{"derivedFrom":sQuery(id+"F64.wireOp",EDGE,"E34")}),-1.0]])]});
            var Q2;
            Q2=makeQuery(id+"F64.imprint","IMPRINT",FACE,{"disambiguationData":[TD([[makeQuery(id+"F64.imprint","IMPRINT",EDGE,{"derivedFrom":sQuery(id+"F64.wireOp",EDGE,"E35")}),1.0]])]});
            var Q3;
            Q3=makeQuery(id+"F64.imprint","IMPRINT",FACE,{"disambiguationData":[TD([[makeQuery(id+"F64.imprint","IMPRINT",EDGE,{"derivedFrom":sQuery(id+"F64.wireOp",EDGE,"E32")}),-1.0]])]});
            var Q4;
            Q4=makeQuery(id+"F64.imprint","IMPRINT",FACE,{"disambiguationData":[TD([[makeQuery(id+"F64.imprint","IMPRINT",EDGE,{"derivedFrom":sQuery(id+"F64.wireOp",EDGE,"E32")}),1.0]])]});
            extrude(context, id + "F67", {"entities" : qUnion([Q0, Q1, Q2, Q3, Q4]), "depth" : 0.53 * mm});
        }
        {
            var Q0;
            Q0=qCreatedBy(id+"F61.planeOp",FACE);
            cPlane(context, id + "F68", {"entities" : qUnion([Q0]), "cplaneType" : CPlaneType.OFFSET, "offset" : 2.54 * mm, "oppositeDirection" : true, "width" : 152.4 * mm, "height" : 152.4 * mm});
        }
        {
            var Q0;
            Q0=qCreatedBy(id+"F15.planeOp",FACE);
            cPlane(context, id + "F69", {"entities" : qUnion([Q0]), "cplaneType" : CPlaneType.OFFSET, "offset" : 2.54 * mm, "width" : 152.4 * mm, "height" : 152.4 * mm});
        }
        {
            var Q0;
            Q0=qCreatedBy(id+"F69.planeOp",FACE);
            cPlane(context, id + "F70", {"entities" : qUnion([Q0]), "cplaneType" : CPlaneType.OFFSET, "offset" : 2.54 * mm, "width" : 152.4 * mm, "height" : 152.4 * mm});
        }
        {
            var Q0;
            Q0=qCreatedBy(id+"F70.planeOp",FACE);
            cPlane(context, id + "F71", {"entities" : qUnion([Q0]), "cplaneType" : CPlaneType.OFFSET, "offset" : 25.4 * mm, "width" : 152.4 * mm, "height" : 152.4 * mm});
        }
    });
